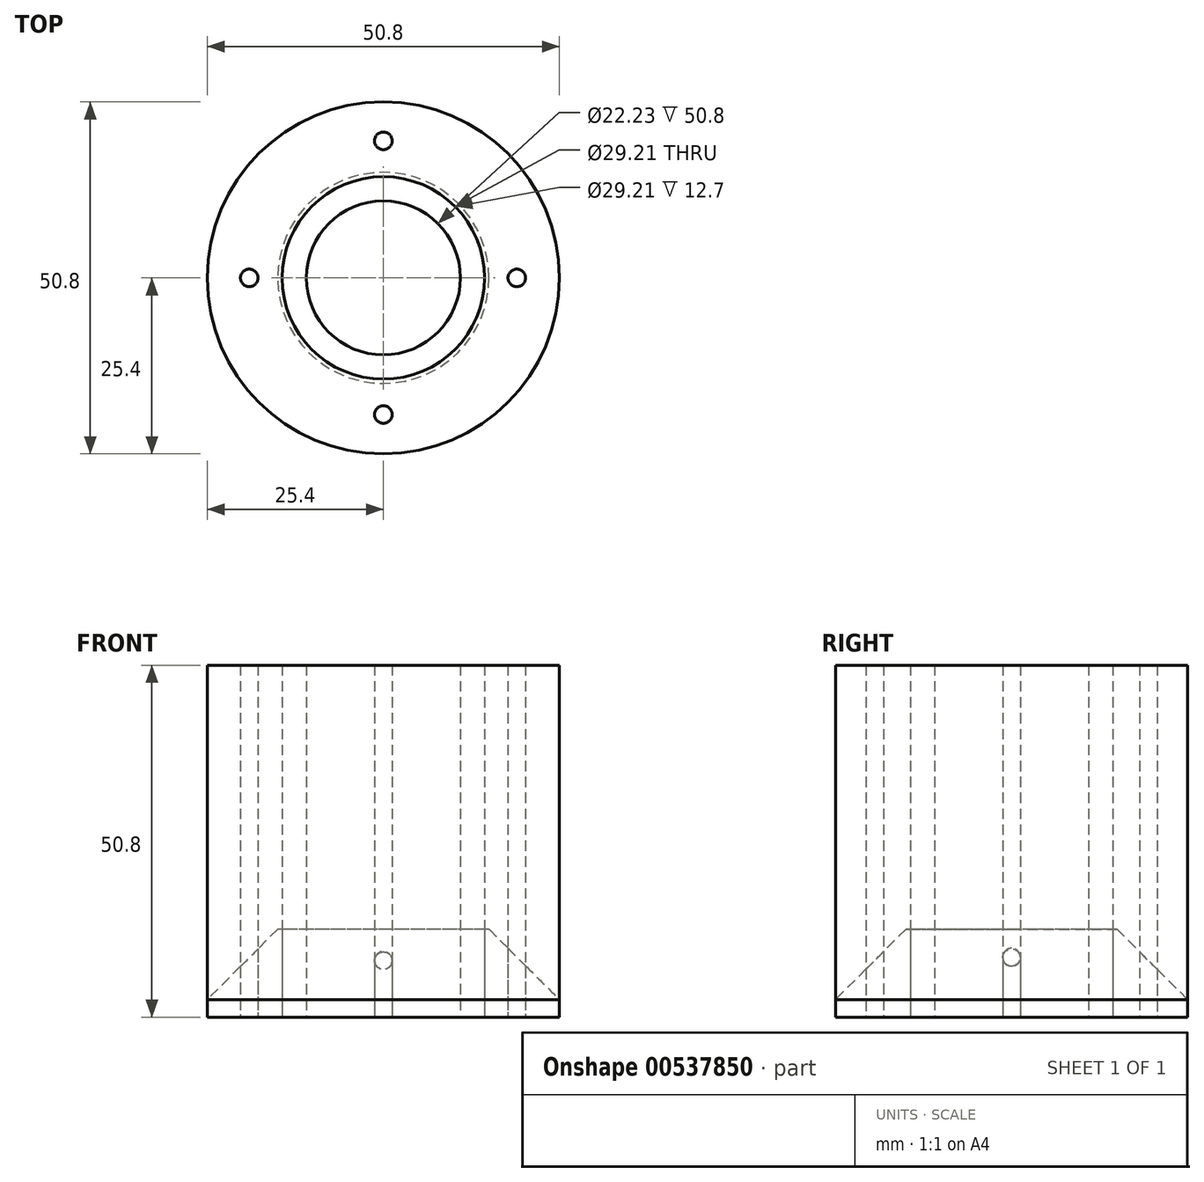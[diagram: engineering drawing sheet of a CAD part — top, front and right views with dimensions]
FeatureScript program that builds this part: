
annotation { "Feature Type Name" : "Feature", "Feature Type Description" : "" }
export const myFeature = defineFeature(function(context is Context, id is Id, definition is map)
    precondition{}
    {
        {
            var Q0;
            Q0=qCreatedBy(makeId("Top.planeOp"),FACE);
            var sketch = newSketch(context, id + "F0", { "sketchPlane" : qUnion([Q0])});
            skCircle(sketch, "E0", {"center": v(0, 0) * mm, "radius": 25.4 * mm});
            skCircle(sketch, "E1", {"center": v(0, 0) * mm, "radius": 11.11 * mm});
            skCircle(sketch, "E2", {"center": v(0, 19.8) * mm, "radius": 1.27 * mm});
            skCircle(sketch, "E3", {"center": v(0, -19.72) * mm, "radius": 1.27 * mm});
            skCircle(sketch, "E4", {"center": v(-19.36, 0) * mm, "radius": 1.27 * mm});
            skCircle(sketch, "E5", {"center": v(19.26, 0) * mm, "radius": 1.27 * mm});
            skCircle(sketch, "E6", {"center": v(0, 0) * mm, "radius": 14.6 * mm});
            skSolve(sketch);
        }
        {
            var Q0;
            Q0=makeQuery(id+"F0.imprint","IMPRINT",FACE,{"disambiguationData":[TD([[makeQuery(id+"F0.imprint","IMPRINT",EDGE,{"derivedFrom":sQuery(id+"F0.wireOp",EDGE,"E0")}),1.0]])]});
            extrude(context, id + "F1", {"entities" : qUnion([Q0]), "depth" : 12.7 * mm, "offsetDistance" : 25.4 * mm});
        }
        {
            var Q0;
            Q0=makeQuery(id+"F0.imprint","IMPRINT",FACE,{"disambiguationData":[TD([[makeQuery(id+"F0.imprint","IMPRINT",EDGE,{"derivedFrom":sQuery(id+"F0.wireOp",EDGE,"E1")}),-1.0]])]});
            extrude(context, id + "F2", {"entities" : qUnion([Q0]), "depth" : 50.8 * mm, "offsetDistance" : 25.4 * mm});
        }
        {
            var Q0;
            Q0=makeQuery(id+"F1.opExtrude","CAP_EDGE",EDGE,{"disambiguationData":[OSD([sQuery(id+"F0.wireOp",EDGE,"E0")])],"isStart":false});
            chamfer(context, id + "F3", {"entities" : qUnion([Q0]), "width" : 10.16 * mm, "tangentPropagation" : true});
        }
        {
            var Q0;
            Q0=makeQuery(id+"F0.imprint","IMPRINT",FACE,{"disambiguationData":[TD([[makeQuery(id+"F0.imprint","IMPRINT",EDGE,{"derivedFrom":sQuery(id+"F0.wireOp",EDGE,"E0")}),1.0]])]});
            extrude(context, id + "F4", {"entities" : qUnion([Q0]), "depth" : 50.8 * mm, "offsetDistance" : 25.4 * mm});
        }
    });
